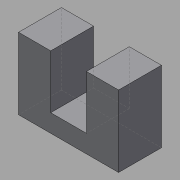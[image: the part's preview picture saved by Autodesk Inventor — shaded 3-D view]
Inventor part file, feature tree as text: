
AUTODESK INVENTOR PART (.ipt)
format: ipt  version: 2015 (Build 190159000, 159)  size: 78,336 bytes
history: native  units: in
note: dims shown in document units (in); Inventor stores cm internally (conversion verified against a paired STEP export)
features: other x3, sketch x2
ambient origin geometry x8: Origin, YZ Plane, XZ Plane, XY Plane, X Axis, Y Axis, Z Axis, Center Point
bodies: Solid1 (feature_tree)
feature tree (5):
  other  "opto.ipt"
  other  "Solid1::opto.ipt"
  other  "TaggingFeature1"
  sketch  "Sketch1"  dims[d0=0.3937in]
  sketch  "Sketch2"
